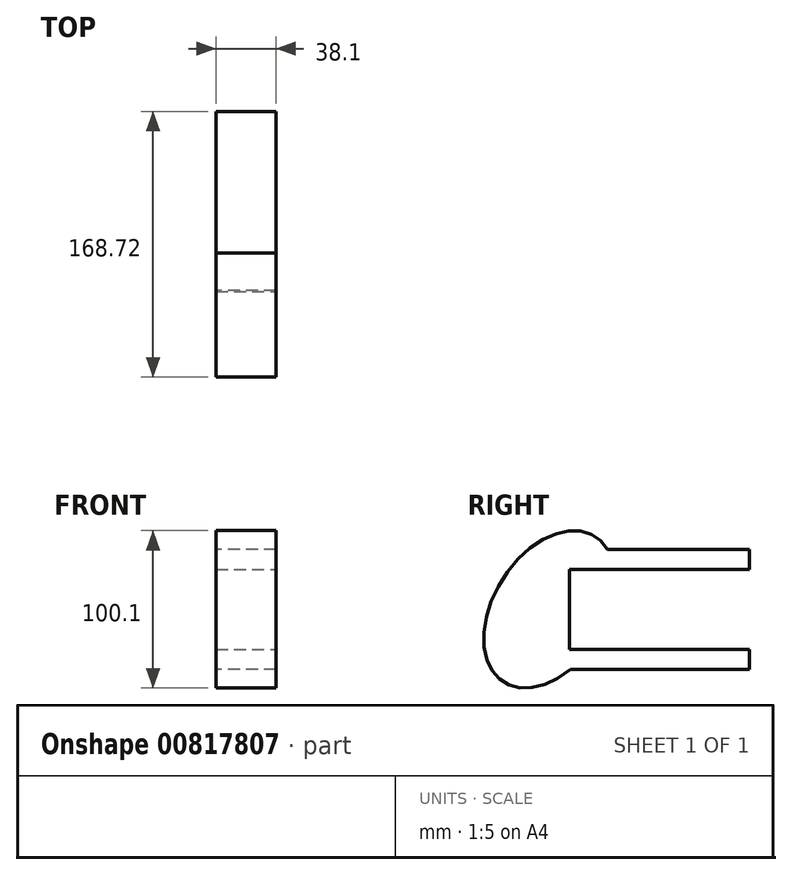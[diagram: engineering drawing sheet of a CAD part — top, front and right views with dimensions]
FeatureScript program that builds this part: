
annotation { "Feature Type Name" : "Feature", "Feature Type Description" : "" }
export const myFeature = defineFeature(function(context is Context, id is Id, definition is map)
    precondition{}
    {
        {
            var Q0;
            Q0=qCreatedBy(makeId("Right.planeOp"),FACE);
            var sketch = newSketch(context, id + "F0", { "sketchPlane" : qUnion([Q0])});
            skLineSegment(sketch, "E0.bottom", {"start": v(0, 38.1) * mm, "end": v(127, 38.1) * mm});
            skLineSegment(sketch, "E0.top", {"start": v(0, -38.1) * mm, "end": v(127, -38.1) * mm});
            skLineSegment(sketch, "E0.left", {"start": v(0, 38.1) * mm, "end": v(0, -38.1) * mm});
            skLineSegment(sketch, "E0.right", {"start": v(127, 38.1) * mm, "end": v(127, -38.1) * mm});
            skSolve(sketch);
        }
        {
            var Q0;
            Q0=makeQuery(id+"F0.imprint","IMPRINT",FACE,{"disambiguationData":[TD([[makeQuery(id+"F0.imprint","IMPRINT",EDGE,{"derivedFrom":sQuery(id+"F0.wireOp",EDGE,"E0.bottom")}),-1.0]])]});
            extrude(context, id + "F1", {"entities" : qUnion([Q0]), "depth" : 38.1 * mm, "offsetDistance" : 25.4 * mm});
        }
        {
            var Q0;
            Q0=qCreatedBy(makeId("Right.planeOp"),FACE);
            var sketch = newSketch(context, id + "F2", { "sketchPlane" : qUnion([Q0])});
            skCircle(sketch, "E1", {"center": v(0, 0) * mm, "radius": 45.72 * mm});
            skSolve(sketch);
        }
        {
            var Q0;
            Q0=makeQuery(id+"F1.opExtrude","CAP_FACE",FACE,{"disambiguationData":[OSD([sQuery(id+"F0.wireOp",EDGE,"E0.bottom"),sQuery(id+"F0.wireOp",EDGE,"E0.top"),sQuery(id+"F0.wireOp",EDGE,"E0.left"),sQuery(id+"F0.wireOp",EDGE,"E0.right")])],"isStart":false});
            var sketch = newSketch(context, id + "F3", { "sketchPlane" : qUnion([Q0])});
            skLineSegment(sketch, "E2.bottom", {"start": v(12.7, 25.4) * mm, "end": v(127, 25.4) * mm});
            skLineSegment(sketch, "E2.top", {"start": v(12.7, -25.4) * mm, "end": v(127, -25.4) * mm});
            skLineSegment(sketch, "E2.left", {"start": v(12.7, 25.4) * mm, "end": v(12.7, -25.4) * mm});
            skLineSegment(sketch, "E2.right", {"start": v(127, 25.4) * mm, "end": v(127, -25.4) * mm});
            skPoint(sketch, "E3", {"position": v(12.7, 0) * mm});
            skLineSegment(sketch, "E4", {"start": v(63.5, 38.1) * mm, "end": v(63.5, 25.4) * mm, "construction": true});
            skLineSegment(sketch, "E5", {"start": v(63.5, -25.4) * mm, "end": v(63.5, -38.1) * mm, "construction": true});
            skLineSegment(sketch, "E6", {"start": v(12.7, 0) * mm, "end": v(0, 0) * mm, "construction": true});
            skSolve(sketch);
        }
        {
            var Q0;
            Q0=qCreatedBy(makeId("Right.planeOp"),FACE);
            var sketch = newSketch(context, id + "F4", { "sketchPlane" : qUnion([Q0])});
            skEllipse(sketch, "E7", {"center": v(0, 0) * mm, "majorRadius": 54.66 * mm, "minorRadius": 35.46 * mm, "majorAxis": v(-0.53, -0.85)});
            skSolve(sketch);
        }
        {
            var Q0;
            Q0=makeQuery(id+"F4.imprint","IMPRINT",FACE,{"disambiguationData":[TD([[makeQuery(id+"F4.imprint","IMPRINT",EDGE,{"derivedFrom":sQuery(id+"F4.wireOp",EDGE,"E7")}),1.0]])]});
            var Q1;
            Q1=makeQuery(id+"F1.opExtrude","CAP_FACE",FACE,{"disambiguationData":[OSD([sQuery(id+"F0.wireOp",EDGE,"E0.bottom"),sQuery(id+"F0.wireOp",EDGE,"E0.top"),sQuery(id+"F0.wireOp",EDGE,"E0.left"),sQuery(id+"F0.wireOp",EDGE,"E0.right")])],"isStart":false});
            extrude(context, id + "F5", {"entities" : qUnion([Q0]), "operationType" : NewBodyOperationType.ADD, "endBound" : BoundingType.UP_TO_SURFACE, "depth" : 25.4 * mm, "endBoundEntityFace" : qUnion([Q1]), "offsetDistance" : 25.4 * mm});
        }
        {
            var Q0;
            Q0 = qSketchRegion(id + "F3", true);
            extrude(context, id + "F6", {"entities" : qUnion([Q0]), "operationType" : NewBodyOperationType.REMOVE, "endBound" : BoundingType.THROUGH_ALL, "oppositeDirection" : true, "depth" : 25.4 * mm, "offsetDistance" : 25.4 * mm});
        }
    });
